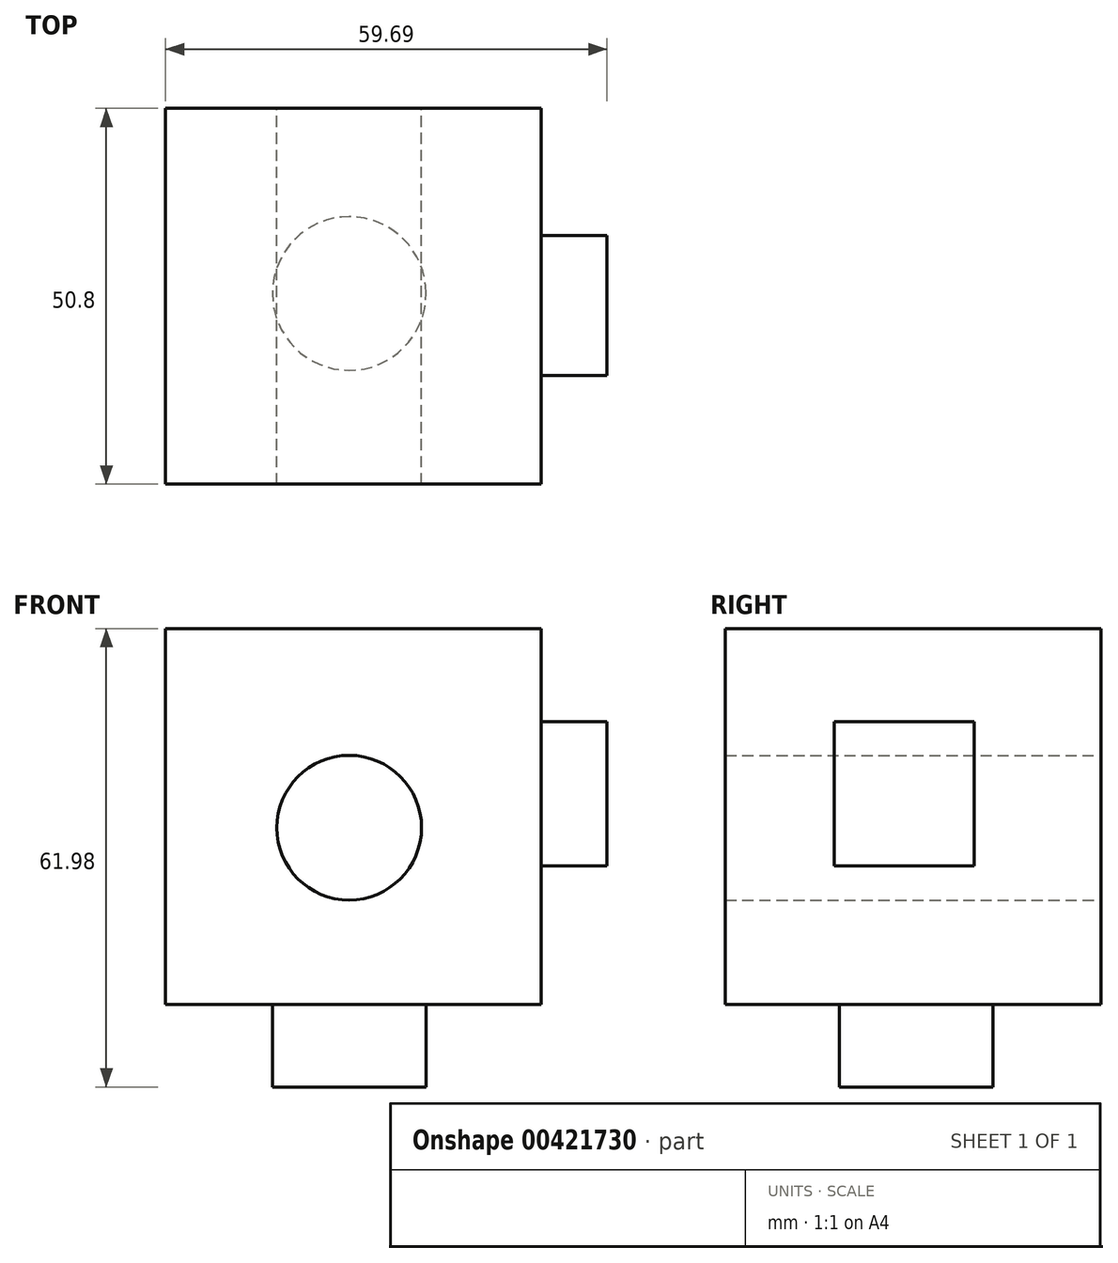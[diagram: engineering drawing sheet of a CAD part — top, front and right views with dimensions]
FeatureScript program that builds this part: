
annotation { "Feature Type Name" : "Feature", "Feature Type Description" : "" }
export const myFeature = defineFeature(function(context is Context, id is Id, definition is map)
    precondition{}
    {
        {
            var Q0;
            Q0=qCreatedBy(makeId("Front.planeOp"),FACE);
            var sketch = newSketch(context, id + "F0", { "sketchPlane" : qUnion([Q0])});
            skLineSegment(sketch, "E0.bottom", {"start": v(0, 0) * mm, "end": v(-50.8, 0) * mm});
            skLineSegment(sketch, "E0.top", {"start": v(0, 50.8) * mm, "end": v(-50.8, 50.8) * mm});
            skLineSegment(sketch, "E0.left", {"start": v(0, 0) * mm, "end": v(0, 50.8) * mm});
            skLineSegment(sketch, "E0.right", {"start": v(-50.8, 0) * mm, "end": v(-50.8, 50.8) * mm});
            skCircle(sketch, "E1", {"center": v(-25.97, 23.87) * mm, "radius": 9.78 * mm});
            skSolve(sketch);
        }
        {
            var Q0;
            Q0=makeQuery(id+"F0.imprint","IMPRINT",FACE,{"disambiguationData":[TD([[makeQuery(id+"F0.imprint","IMPRINT",EDGE,{"derivedFrom":sQuery(id+"F0.wireOp",EDGE,"E0.bottom")}),-1.0]])]});
            extrude(context, id + "F1", {"entities" : qUnion([Q0]), "depth" : 50.8 * mm});
        }
        {
            var Q0;
            Q0=makeQuery(id+"F1.opExtrude","SWEPT_FACE",FACE,{"disambiguationData":[OSD([sQuery(id+"F0.wireOp",EDGE,"E0.left")])]});
            var sketch = newSketch(context, id + "F2", { "sketchPlane" : qUnion([Q0])});
            skLineSegment(sketch, "E2.bottom", {"start": v(-17.19, 18.71) * mm, "end": v(-36.1, 18.71) * mm});
            skLineSegment(sketch, "E2.top", {"start": v(-17.19, 38.2) * mm, "end": v(-36.1, 38.2) * mm});
            skLineSegment(sketch, "E2.left", {"start": v(-17.19, 18.71) * mm, "end": v(-17.19, 38.2) * mm});
            skLineSegment(sketch, "E2.right", {"start": v(-36.1, 18.71) * mm, "end": v(-36.1, 38.2) * mm});
            skSolve(sketch);
        }
        {
            var Q0;
            Q0=makeQuery(id+"F2.imprint","IMPRINT",FACE,{"disambiguationData":[TD([[makeQuery(id+"F2.imprint","IMPRINT",EDGE,{"derivedFrom":sQuery(id+"F2.wireOp",EDGE,"E2.bottom")}),-1.0]])]});
            extrude(context, id + "F3", {"entities" : qUnion([Q0]), "operationType" : NewBodyOperationType.ADD, "depth" : 8.64 * mm});
        }
        {
            var Q0;
            Q0=makeQuery(id+"F2.imprint","IMPRINT",FACE,{"disambiguationData":[TD([[makeQuery(id+"F2.imprint","IMPRINT",EDGE,{"derivedFrom":sQuery(id+"F2.wireOp",EDGE,"E2.bottom")}),-1.0]])]});
            extrude(context, id + "F4", {"entities" : qUnion([Q0]), "operationType" : NewBodyOperationType.ADD, "depth" : 8.9 * mm});
        }
        {
            var Q0;
            Q0=makeQuery(id+"F1.opExtrude","SWEPT_FACE",FACE,{"disambiguationData":[OSD([sQuery(id+"F0.wireOp",EDGE,"E0.bottom")])]});
            var sketch = newSketch(context, id + "F5", { "sketchPlane" : qUnion([Q0])});
            skCircle(sketch, "E3", {"center": v(-25.97, 25.02) * mm, "radius": 10.39 * mm});
            skSolve(sketch);
        }
        {
            var Q0;
            Q0=makeQuery(id+"F5.imprint","IMPRINT",FACE,{"disambiguationData":[TD([[makeQuery(id+"F5.imprint","IMPRINT",EDGE,{"derivedFrom":sQuery(id+"F5.wireOp",EDGE,"E3")}),1.0]])]});
            extrude(context, id + "F6", {"entities" : qUnion([Q0]), "operationType" : NewBodyOperationType.ADD, "depth" : 11.18 * mm});
        }
    });
